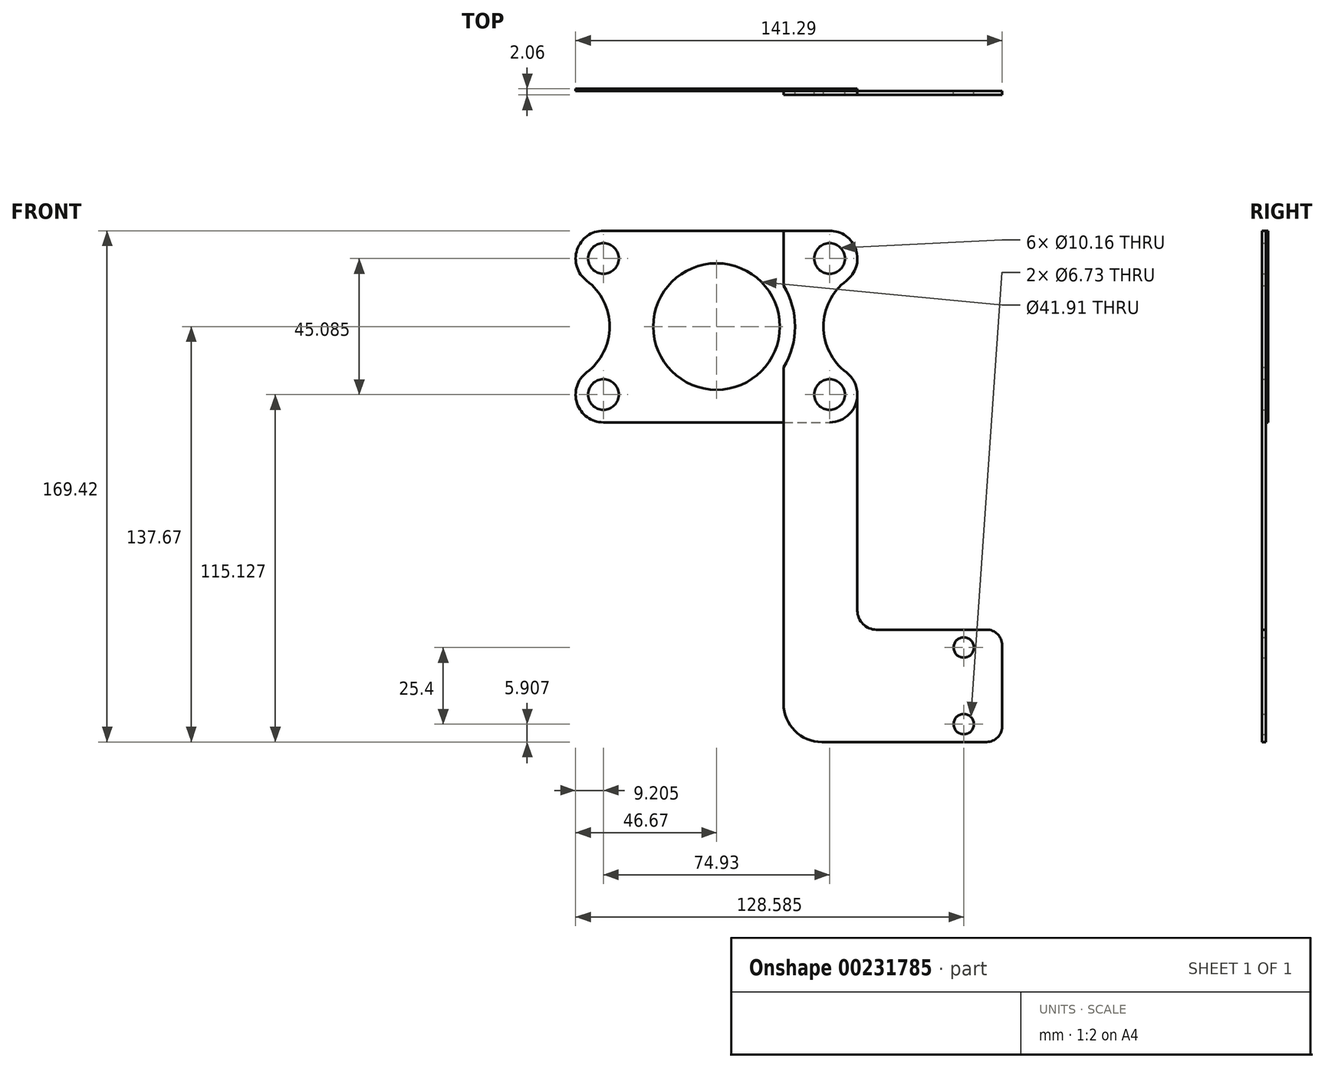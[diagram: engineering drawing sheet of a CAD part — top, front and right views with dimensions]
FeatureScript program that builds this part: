
annotation { "Feature Type Name" : "Feature", "Feature Type Description" : "" }
export const myFeature = defineFeature(function(context is Context, id is Id, definition is map)
    precondition{}
    {
        {
            var Q0;
            Q0=qCreatedBy(makeId("Front.planeOp"),FACE);
            var sketch = newSketch(context, id + "F0", { "sketchPlane" : qUnion([Q0])});
            skLineSegment(sketch, "E0.bottom", {"start": v(-37.47, 31.75) * mm, "end": v(37.46, 31.75) * mm});
            skLineSegment(sketch, "E0.top", {"start": v(-37.46, -31.75) * mm, "end": v(37.47, -31.75) * mm});
            skPoint(sketch, "E0.middle", {"position": v(0, 0) * mm});
            skCircle(sketch, "E1", {"center": v(-37.46, 22.54) * mm, "radius": 5.08 * mm});
            skCircle(sketch, "E2", {"center": v(37.46, 22.54) * mm, "radius": 5.08 * mm});
            skCircle(sketch, "E3", {"center": v(37.46, -22.54) * mm, "radius": 5.08 * mm});
            skCircle(sketch, "E4", {"center": v(-37.46, -22.54) * mm, "radius": 5.08 * mm});
            skLineSegment(sketch, "E5.bottom", {"start": v(-37.46, 22.54) * mm, "end": v(37.46, 22.54) * mm, "construction": true});
            skLineSegment(sketch, "E5.top", {"start": v(-37.46, -22.54) * mm, "end": v(37.46, -22.54) * mm, "construction": true});
            skLineSegment(sketch, "E5.left", {"start": v(-37.46, 22.54) * mm, "end": v(-37.46, -22.54) * mm, "construction": true});
            skLineSegment(sketch, "E5.right", {"start": v(37.46, 22.54) * mm, "end": v(37.46, -22.54) * mm, "construction": true});
            skLineSegment(sketch, "E6", {"start": v(-35.43, 0) * mm, "end": v(35.43, 0) * mm, "construction": true});
            skPoint(sketch, "E7.visualSharp", {"position": v(-46.67, 31.75) * mm});
            skArc(sketch, "E7.filletArc", {"start": v(-37.47, 31.75) * mm, "mid": v(-43.98, 29.05) * mm, "end": v(-46.67, 22.54) * mm});
            skPoint(sketch, "E8.visualSharp", {"position": v(46.67, 31.75) * mm});
            skArc(sketch, "E8.filletArc", {"start": v(46.67, 22.54) * mm, "mid": v(43.98, 29.05) * mm, "end": v(37.46, 31.75) * mm});
            skPoint(sketch, "E9.visualSharp", {"position": v(46.67, -31.75) * mm});
            skArc(sketch, "E9.filletArc", {"start": v(37.47, -31.75) * mm, "mid": v(43.98, -29.05) * mm, "end": v(46.67, -22.54) * mm});
            skPoint(sketch, "E10.visualSharp", {"position": v(-46.67, -31.75) * mm});
            skArc(sketch, "E10.filletArc", {"start": v(-46.67, -22.54) * mm, "mid": v(-43.98, -29.05) * mm, "end": v(-37.46, -31.75) * mm});
            skCircle(sketch, "E11", {"center": v(0, 0) * mm, "radius": 20.96 * mm});
            skArc(sketch, "E12", {"start": v(-43, -15.19) * mm, "mid": v(-35.43, 0) * mm, "end": v(-43, 15.19) * mm});
            skArc(sketch, "E13", {"start": v(-37.47, 31.75) * mm, "mid": v(-46.2, 25.46) * mm, "end": v(-43, 15.19) * mm});
            skArc(sketch, "E14", {"start": v(-43, -15.19) * mm, "mid": v(-46.2, -25.46) * mm, "end": v(-37.46, -31.75) * mm});
            skArc(sketch, "E15", {"start": v(43, 15.19) * mm, "mid": v(46.2, 25.46) * mm, "end": v(37.46, 31.75) * mm});
            skArc(sketch, "E16", {"start": v(37.47, -31.75) * mm, "mid": v(46.2, -25.46) * mm, "end": v(43, -15.19) * mm});
            skArc(sketch, "E17", {"start": v(43, 15.19) * mm, "mid": v(35.43, 0) * mm, "end": v(43, -15.19) * mm});
            skSolve(sketch);
        }
        {
            var Q0;
            Q0=qSketchRegion(id+"F0",true);
            extrude(context, id + "F1", {"entities" : qUnion([Q0]), "depth" : 0.8 * mm});
        }
        {
            var Q0;
            Q0=makeQuery(id+"F1.opExtrude","CAP_FACE",FACE,{"disambiguationData":[OSD([sQuery(id+"F0.wireOp",EDGE,"E0.bottom"),sQuery(id+"F0.wireOp",EDGE,"E0.top"),sQuery(id+"F0.wireOp",EDGE,"E1"),sQuery(id+"F0.wireOp",EDGE,"E2"),sQuery(id+"F0.wireOp",EDGE,"E3"),sQuery(id+"F0.wireOp",EDGE,"E4"),sQuery(id+"F0.wireOp",EDGE,"E11"),sQuery(id+"F0.wireOp",EDGE,"E12"),sQuery(id+"F0.wireOp",EDGE,"E13"),sQuery(id+"F0.wireOp",EDGE,"E14"),sQuery(id+"F0.wireOp",EDGE,"E15"),sQuery(id+"F0.wireOp",EDGE,"E16"),sQuery(id+"F0.wireOp",EDGE,"E17")])],"isStart":false});
            var sketch = newSketch(context, id + "F2", { "sketchPlane" : qUnion([Q0])});
            skCircle(sketch, "E18.0", {"center": v(37.46, 22.54) * mm, "radius": 5.08 * mm});
            skCircle(sketch, "E19.0", {"center": v(37.46, -22.54) * mm, "radius": 5.08 * mm});
            skCircle(sketch, "E20.0", {"center": v(0, 0) * mm, "radius": 20.96 * mm, "construction": true});
            skArc(sketch, "E21.0", {"start": v(43, 15.19) * mm, "mid": v(35.43, 0) * mm, "end": v(43, -15.19) * mm});
            skArc(sketch, "E22.0", {"start": v(43, 15.19) * mm, "mid": v(46.2, 25.46) * mm, "end": v(37.46, 31.75) * mm});
            skArc(sketch, "E23.0", {"start": v(46.67, -22.54) * mm, "mid": v(45.7, -18.43) * mm, "end": v(43, -15.19) * mm});
            skLineSegment(sketch, "E24", {"start": v(22.22, 31.75) * mm, "end": v(22.23, 13.56) * mm});
            skLineSegment(sketch, "E25", {"start": v(22.22, 31.75) * mm, "end": v(37.46, 31.75) * mm});
            skCircle(sketch, "E26", {"center": v(81.91, -106.36) * mm, "radius": 3.37 * mm});
            skCircle(sketch, "E27", {"center": v(81.91, -131.76) * mm, "radius": 3.37 * mm});
            skLineSegment(sketch, "E28", {"start": v(81.91, -106.36) * mm, "end": v(81.91, -131.76) * mm, "construction": true});
            skLineSegment(sketch, "E29", {"start": v(94.62, -137.67) * mm, "end": v(34.93, -137.67) * mm});
            skLineSegment(sketch, "E30", {"start": v(94.61, -100.46) * mm, "end": v(53.02, -100.46) * mm});
            skLineSegment(sketch, "E31", {"start": v(46.67, -22.54) * mm, "end": v(46.67, -94.1) * mm});
            skPoint(sketch, "E32.visualSharp", {"position": v(46.67, -100.46) * mm});
            skArc(sketch, "E32.filletArc", {"start": v(46.67, -94.1) * mm, "mid": v(48.53, -98.6) * mm, "end": v(53.02, -100.46) * mm});
            skPoint(sketch, "E33.visualSharp", {"position": v(22.23, -137.67) * mm});
            skArc(sketch, "E33.filletArc", {"start": v(22.23, -124.97) * mm, "mid": v(25.94, -133.95) * mm, "end": v(34.93, -137.67) * mm});
            skLineSegment(sketch, "E34", {"start": v(94.61, -100.46) * mm, "end": v(94.62, -137.67) * mm});
            skPoint(sketch, "E35.orphan", {"position": v(37.47, -31.75) * mm});
            skArc(sketch, "E36", {"start": v(22.23, -13.56) * mm, "mid": v(26.04, 0) * mm, "end": v(22.23, 13.56) * mm});
            skLineSegment(sketch, "E37.trimOffspring", {"start": v(22.23, -13.56) * mm, "end": v(22.23, -124.97) * mm});
            skSolve(sketch);
        }
        {
            var Q0;
            Q0=qSketchRegion(id+"F2",true);
            extrude(context, id + "F3", {"entities" : qUnion([Q0]), "depth" : 1.27 * mm});
        }
        {
            var Q0;
            Q0=makeQuery(id+"F3.opExtrude","SWEPT_EDGE",EDGE,{"disambiguationData":[OSD([sQuery(id+"F2.wireOp",EDGE,"E30"),sQuery(id+"F2.wireOp",EDGE,"E34")])]});
            var Q1;
            Q1=makeQuery(id+"F3.opExtrude","SWEPT_EDGE",EDGE,{"disambiguationData":[OSD([sQuery(id+"F2.wireOp",EDGE,"E29"),sQuery(id+"F2.wireOp",EDGE,"E34")])]});
            fillet(context, id + "F4", {"entities" : qUnion([Q0, Q1]), "radius" : 5.08 * mm, "tangentPropagation" : true, "allowEdgeOverflow" : false});
        }
    });
